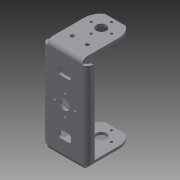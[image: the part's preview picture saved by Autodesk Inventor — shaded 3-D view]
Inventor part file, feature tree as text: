
AUTODESK INVENTOR PART (.ipt)
format: ipt  version: 2013 (Build 170138000, 138)  size: 265,728 bytes
history: native  units: in
note: dims shown in document units (in); Inventor stores cm internally (conversion verified against a paired STEP export)
features: sheet_metal_op x13, sketch x10, other x10, reference x4, chamfer x1, projected_geometry x1
ambient origin geometry x8: Origin, YZ Plane, XZ Plane, XY Plane, X Axis, Y Axis, Z Axis, Center Point
bodies: Solid1 (feature_tree)
feature tree (39):
  sheet_metal_op  "Face1"
  sheet_metal_op  "Flange1"
  sheet_metal_op  "Flange2"
  sheet_metal_op  "Flange3"
  sheet_metal_op  "Flange4"
  chamfer  "Corner Round1"
  sketch  "Sketch1"  dims[d0=1.4173in]
  reference  "Reference1"
  reference  "Reference2"
  reference  "Reference3"
  reference  "Reference4"
  other  "Plate1"
  sketch  "Sketch2"  dims[d1=2.8346in]
  other  "Plate2"
  sheet_metal_op  "Bend1"
  sheet_metal_op  "Corner1"
  sketch  "Sketch3"  dims[d3=0.315in]
  other  "Plate3"
  sheet_metal_op  "Bend2"
  sheet_metal_op  "Corner2"
  sketch  "Sketch4"  dims[d4=0.0787in]
  other  "Plate4"
  sheet_metal_op  "Bend3"
  sheet_metal_op  "Corner3"
  sketch  "Sketch5"  dims[d5=0.0787in]
  other  "Plate5"
  sheet_metal_op  "Bend4"
  sheet_metal_op  "Corner4"
  sketch  "Sketch6"  dims[d6=0.0787in]
  sketch  "Sketch7"  dims[d7=0.0787in]
  projected_geometry  "Projected Loop1"
  sketch  "Sketch8"  dims[d8=0.0787in]
  sketch  "Sketch9"  dims[d9=0.0787in]
  sketch  "Sketch10"  dims[d10=0.0394in d11=0.1575in d12=0.0787in d13=1.5748in d14=90.0deg d15=0.0787in d16=0.315in d17=0.0787in d18=0.0787in d19=0.0787in d20=0.0394in d21=0.1575in d22=0.0787in d23=1.5748in d24=90.0deg d25=0.0787in d26=0.315in d27=0.0787in d28=0.0787in d29=0.0787in d30=0.0394in d31=0.1575in d32=0.0787in d33=0.2362in d34=90.0deg d35=0.0787in d36=0.315in d37=0.0787in d38=0.0787in d39=0.0787in d40=0.0394in d41=0.1575in d42=0.0787in d43=0.2362in d44=90.0deg d45=0.0787in d46=0.315in d47=0.0787in d48=0.0787in d49=0.0787in d52=0.0787in d53=0.0787in d54=0.0787in d55=0.0787in d56=0.315in d57=0.0787in d58=0.0in d59=0.0787in d60=0.0in d63=0.1181in d64=0.1181in d65=0.0787in d66=0.0in d67=0.0787in d68=0.0in d71=0.3937in d72=0.2362in d73=0.0787in d76=0.2362in d77=0.0787in d78=0.0787in d79=0.0in]
  other  "Cut1"
  other  "Cut2"
  other  "Cut3"
  other  "Cut4"
  other  "Cut5"
